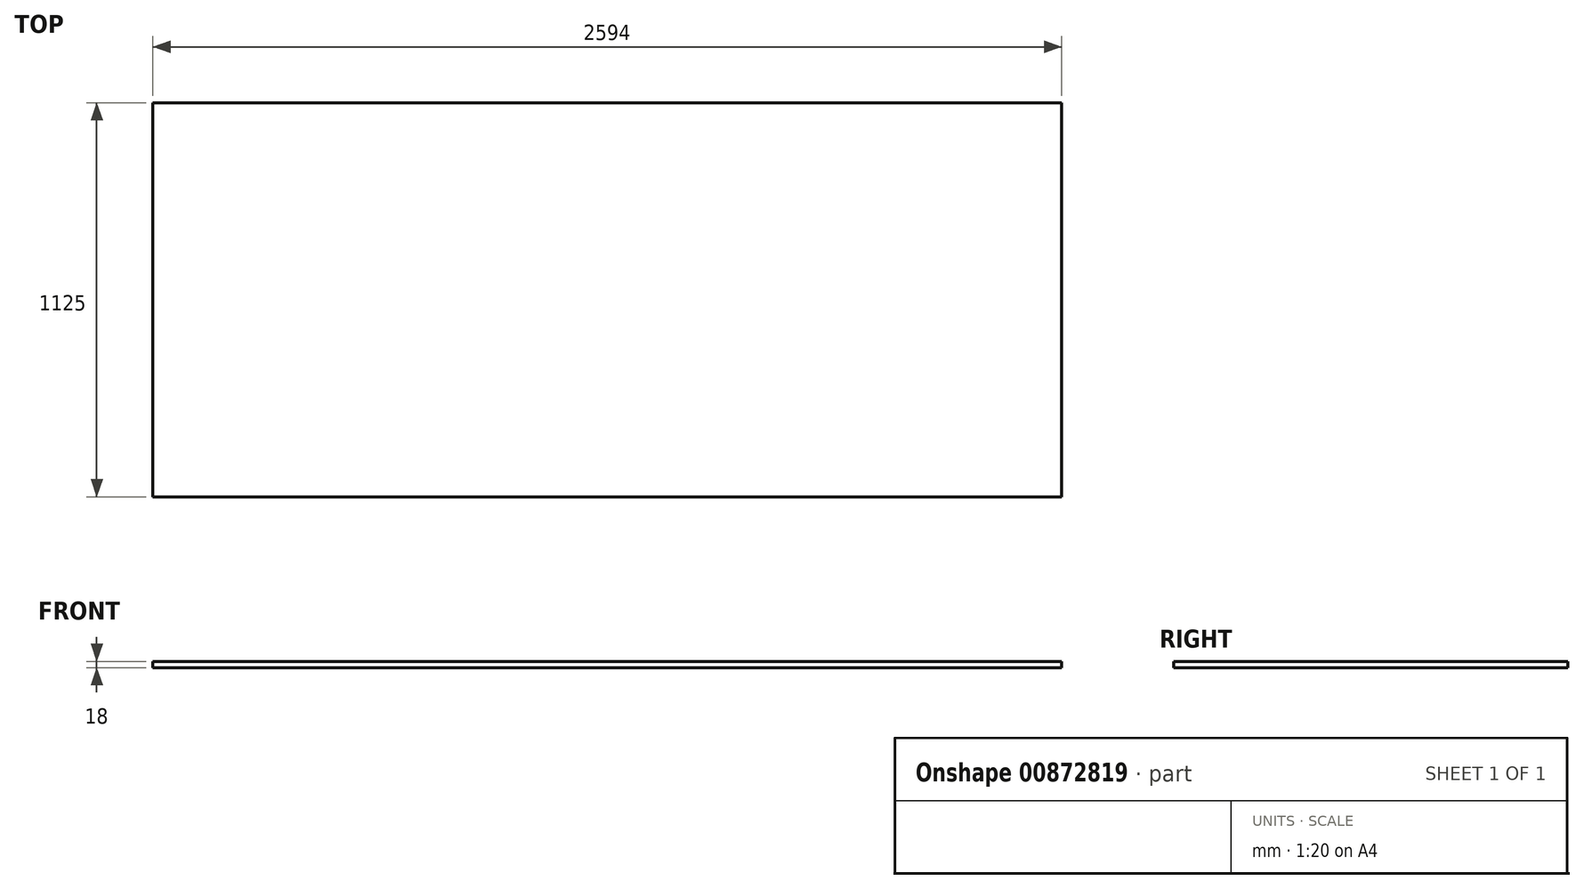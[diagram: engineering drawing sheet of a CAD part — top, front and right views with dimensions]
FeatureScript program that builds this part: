
annotation { "Feature Type Name" : "Feature", "Feature Type Description" : "" }
export const myFeature = defineFeature(function(context is Context, id is Id, definition is map)
    precondition{}
    {
        {
            var Q0;
            Q0=qCreatedBy(makeId("Top.planeOp"),FACE);
            var sketch = newSketch(context, id + "F0", { "sketchPlane" : qUnion([Q0])});
            skLineSegment(sketch, "E0.bottom", {"start": v(1297, -562.5) * mm, "end": v(-1297, -562.5) * mm});
            skLineSegment(sketch, "E0.top", {"start": v(1297, 562.5) * mm, "end": v(-1297, 562.5) * mm});
            skLineSegment(sketch, "E0.left", {"start": v(1297, -562.5) * mm, "end": v(1297, 562.5) * mm});
            skLineSegment(sketch, "E0.right", {"start": v(-1297, -562.5) * mm, "end": v(-1297, 562.5) * mm});
            skPoint(sketch, "E0.middle", {"position": v(0, 0) * mm});
            skSolve(sketch);
        }
        {
            var Q0;
            Q0 = qSketchRegion(id + "F0", true);
            extrude(context, id + "F1", {"entities" : qUnion([Q0]), "depth" : 18 * mm, "offsetDistance" : 25 * mm});
        }
    });
